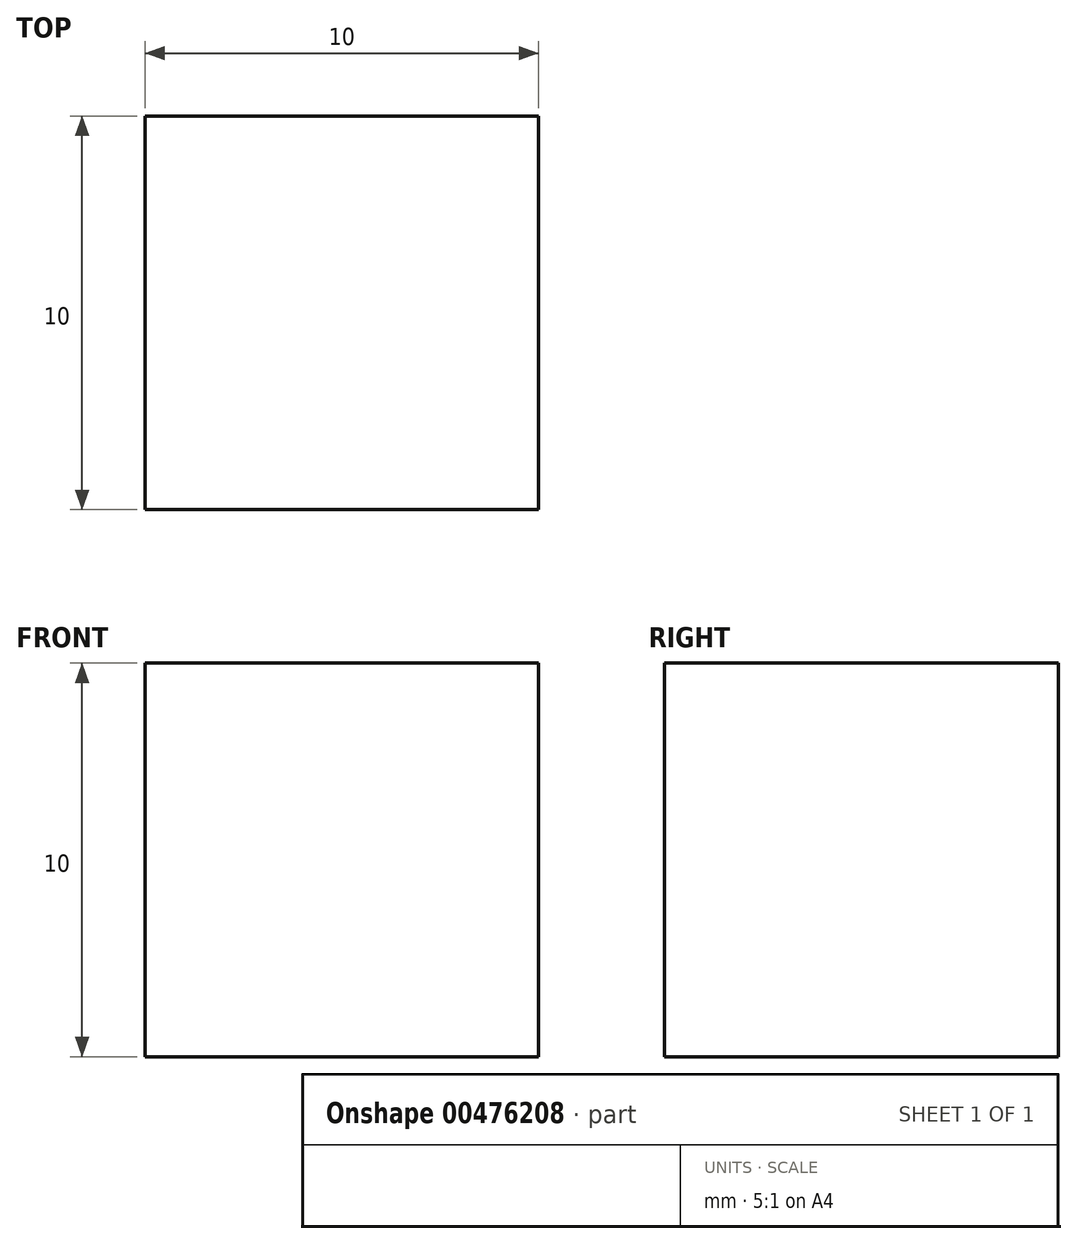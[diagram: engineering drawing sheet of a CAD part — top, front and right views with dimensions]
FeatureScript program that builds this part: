
annotation { "Feature Type Name" : "Feature", "Feature Type Description" : "" }
export const myFeature = defineFeature(function(context is Context, id is Id, definition is map)
    precondition{}
    {
        {
            var Q0;
            Q0=qCreatedBy(makeId("Front.planeOp"),FACE);
            var sketch = newSketch(context, id + "F0", { "sketchPlane" : qUnion([Q0])});
            skLineSegment(sketch, "E0.bottom", {"start": v(0, 0) * mm, "end": v(10, 0) * mm});
            skLineSegment(sketch, "E0.top", {"start": v(0, 10) * mm, "end": v(10, 10) * mm});
            skLineSegment(sketch, "E0.left", {"start": v(0, 0) * mm, "end": v(0, 10) * mm});
            skLineSegment(sketch, "E0.right", {"start": v(10, 0) * mm, "end": v(10, 10) * mm});
            skSolve(sketch);
        }
        {
            var Q0;
            Q0 = qSketchRegion(id + "F0", true);
            extrude(context, id + "F1", {"entities" : qUnion([Q0]), "depth" : 10 * mm});
        }
    });
